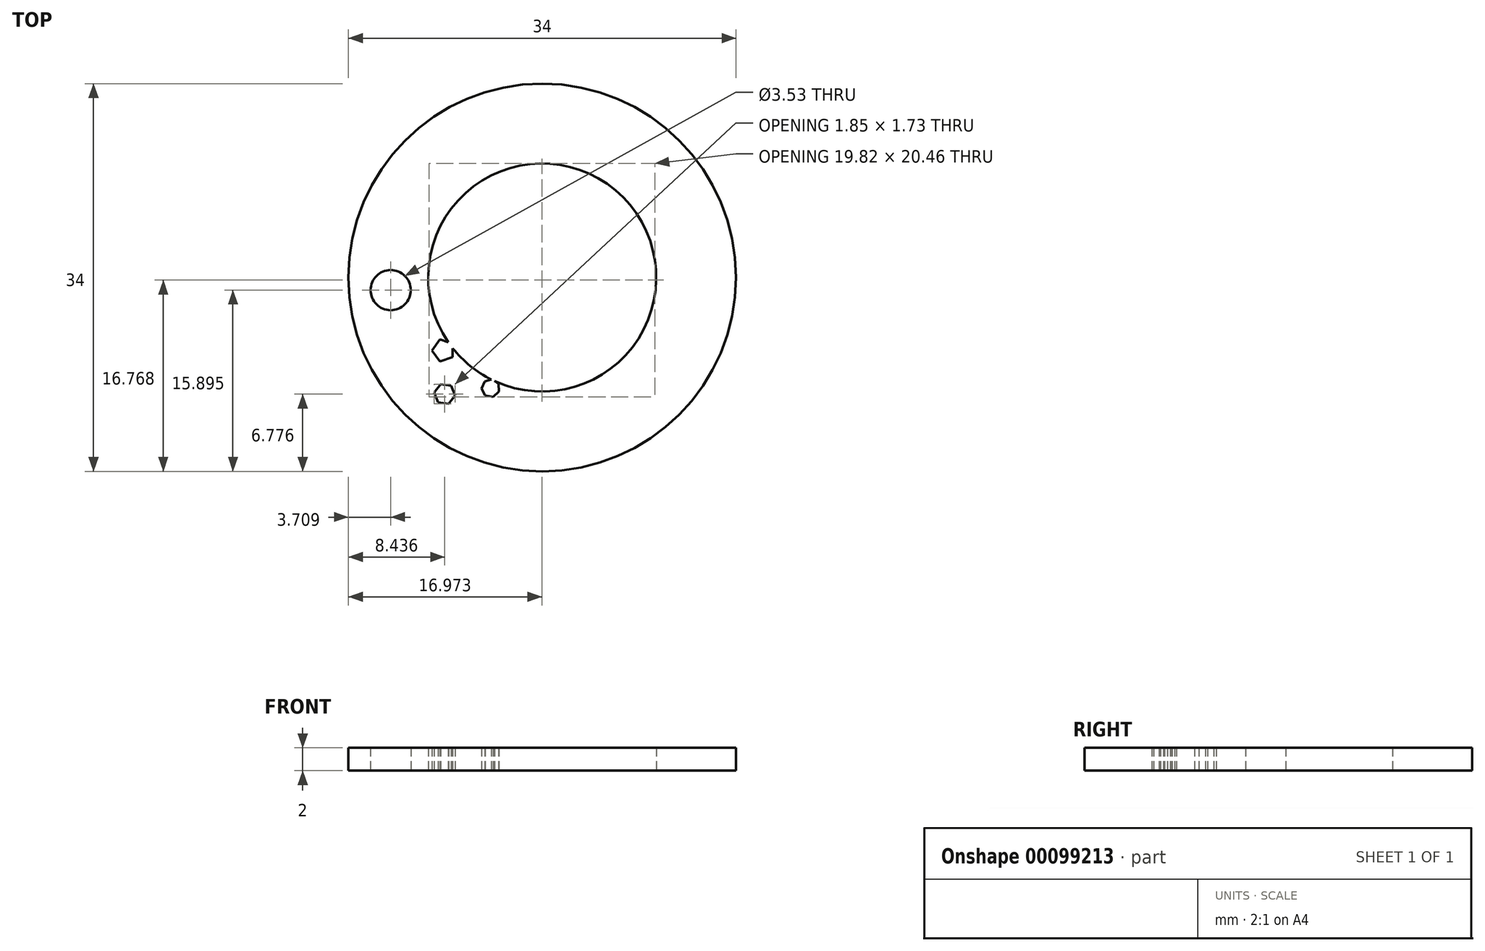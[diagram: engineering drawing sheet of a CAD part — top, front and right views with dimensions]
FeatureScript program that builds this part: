
annotation { "Feature Type Name" : "Feature", "Feature Type Description" : "" }
export const myFeature = defineFeature(function(context is Context, id is Id, definition is map)
    precondition{}
    {
        {
            var Q0;
            Q0=qCreatedBy(makeId("Top.planeOp"),FACE);
            var sketch = newSketch(context, id + "F0", { "sketchPlane" : qUnion([Q0])});
            skCircle(sketch, "E0", {"center": v(-45.42, 0) * mm, "radius": 17 * mm});
            skCircle(sketch, "E1", {"center": v(-45.42, 0) * mm, "radius": 10 * mm});
            skCircle(sketch, "E2.cCircle", {"center": v(-54.08, -6.4) * mm, "radius": 0.82 * mm, "construction": true});
            skLineSegment(sketch, "E2.0", {"start": v(-53.26, -5.8) * mm, "end": v(-53.26, -6.99) * mm});
            skLineSegment(sketch, "E2.1", {"start": v(-53.26, -6.99) * mm, "end": v(-54.4, -7.35) * mm});
            skLineSegment(sketch, "E2.2", {"start": v(-54.4, -7.35) * mm, "end": v(-55.09, -6.4) * mm});
            skLineSegment(sketch, "E2.3", {"start": v(-55.09, -6.4) * mm, "end": v(-54.4, -5.44) * mm});
            skLineSegment(sketch, "E2.4", {"start": v(-54.4, -5.44) * mm, "end": v(-53.26, -5.8) * mm});
            skPoint(sketch, "E2.0.midPoint", {"position": v(-53.26, -6.4) * mm});
            skCircle(sketch, "E3.cCircle", {"center": v(-53.98, -10.22) * mm, "radius": 0.8 * mm, "construction": true});
            skLineSegment(sketch, "E3.0", {"start": v(-53.06, -10.36) * mm, "end": v(-53.64, -11.1) * mm});
            skLineSegment(sketch, "E3.1", {"start": v(-53.64, -11.1) * mm, "end": v(-54.56, -10.96) * mm});
            skLineSegment(sketch, "E3.2", {"start": v(-54.56, -10.96) * mm, "end": v(-54.9, -10.1) * mm});
            skLineSegment(sketch, "E3.3", {"start": v(-54.9, -10.1) * mm, "end": v(-54.33, -9.36) * mm});
            skLineSegment(sketch, "E3.4", {"start": v(-54.33, -9.36) * mm, "end": v(-53.4, -9.5) * mm});
            skLineSegment(sketch, "E3.5", {"start": v(-53.4, -9.5) * mm, "end": v(-53.06, -10.36) * mm});
            skPoint(sketch, "E3.0.midPoint", {"position": v(-53.35, -10.72) * mm});
            skCircle(sketch, "E4.cCircle", {"center": v(-49.95, -9.7) * mm, "radius": 0.7 * mm, "construction": true});
            skLineSegment(sketch, "E4.0", {"start": v(-49.26, -9.33) * mm, "end": v(-49.23, -10.01) * mm});
            skLineSegment(sketch, "E4.1", {"start": v(-49.23, -10.01) * mm, "end": v(-49.74, -10.46) * mm});
            skLineSegment(sketch, "E4.2", {"start": v(-49.74, -10.46) * mm, "end": v(-50.4, -10.34) * mm});
            skLineSegment(sketch, "E4.3", {"start": v(-50.4, -10.34) * mm, "end": v(-50.74, -9.74) * mm});
            skLineSegment(sketch, "E4.4", {"start": v(-50.74, -9.74) * mm, "end": v(-50.47, -9.11) * mm});
            skLineSegment(sketch, "E4.5", {"start": v(-50.47, -9.11) * mm, "end": v(-49.81, -8.93) * mm});
            skLineSegment(sketch, "E4.6", {"start": v(-49.81, -8.93) * mm, "end": v(-49.26, -9.33) * mm});
            skPoint(sketch, "E4.0.midPoint", {"position": v(-49.24, -9.67) * mm});
            skLineSegment(sketch, "E5", {"start": v(-56.67, -11.7) * mm, "end": v(-53.42, -17.79) * mm});
            skLineSegment(sketch, "E6", {"start": v(-53.42, -17.79) * mm, "end": v(-45.6, -13.6) * mm});
            skCircle(sketch, "E7", {"center": v(-45.42, 0) * mm, "radius": 13.34 * mm, "construction": true});
            skCircle(sketch, "E8", {"center": v(-58.71, -1.1) * mm, "radius": 1.76 * mm});
            skSolve(sketch);
        }
        {
            var Q0;
            Q0=makeQuery(id+"F0.imprint","IMPRINT",FACE,{"disambiguationData":[TD([[makeQuery(id+"F0.imprint","IMPRINT",EDGE,{"derivedFrom":sQuery(id+"F0.wireOp",EDGE,"E0")}),1.0]])]});
            extrude(context, id + "F1", {"entities" : qUnion([Q0]), "depth" : 2 * mm});
        }
    });
